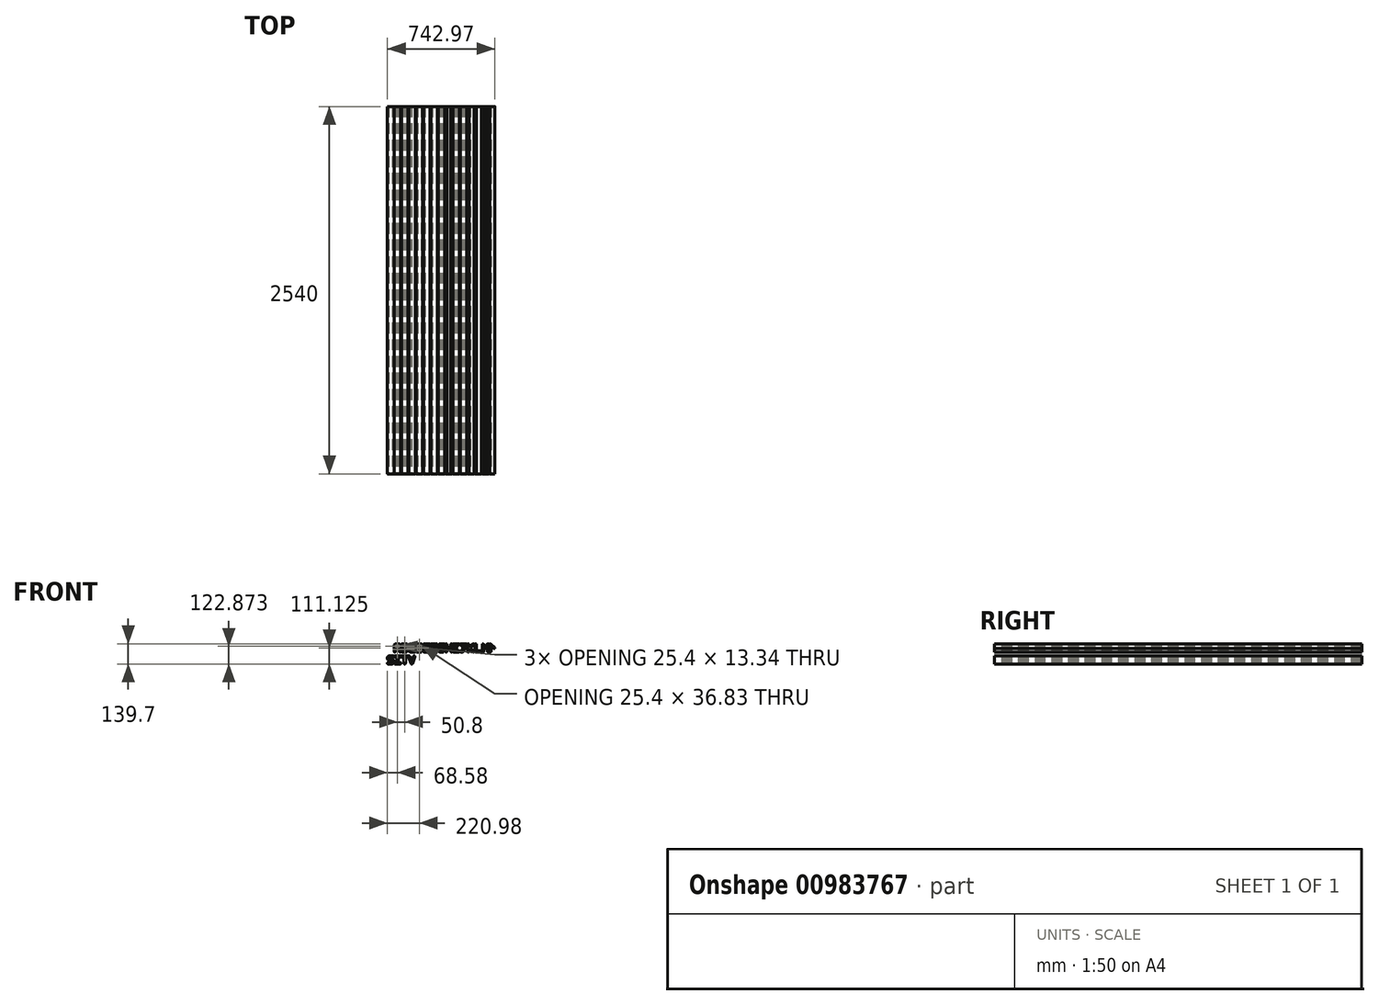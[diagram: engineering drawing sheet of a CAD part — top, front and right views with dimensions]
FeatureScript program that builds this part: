
annotation { "Feature Type Name" : "Feature", "Feature Type Description" : "" }
export const myFeature = defineFeature(function(context is Context, id is Id, definition is map)
    precondition{}
    {
        {
            var Q0;
            Q0=qCreatedBy(makeId("Front.planeOp"),FACE);
            var sketch = newSketch(context, id + "F0", { "sketchPlane" : qUnion([Q0])});
            skLineSegment(sketch, "E0", {"start": v(-40.64, 0) * mm, "end": v(-15.24, 0) * mm});
            skLineSegment(sketch, "E1", {"start": v(0, 0) * mm, "end": v(-15.24, 0) * mm, "construction": true});
            skLineSegment(sketch, "E2", {"start": v(-40.64, 0) * mm, "end": v(-45.72, 0) * mm, "construction": true});
            skLineSegment(sketch, "E3", {"start": v(99.06, -25.4) * mm, "end": v(99.06, -82.55) * mm, "construction": true});
            skLineSegment(sketch, "E4", {"start": v(99.06, -82.55) * mm, "end": v(144.78, -82.55) * mm, "construction": true});
            skPoint(sketch, "E5", {"position": v(121.92, -82.55) * mm});
            skLineSegment(sketch, "E6", {"start": v(99.06, -25.4) * mm, "end": v(144.78, -25.4) * mm, "construction": true});
            skLineSegment(sketch, "E7", {"start": v(144.78, -25.4) * mm, "end": v(144.78, -82.55) * mm, "construction": true});
            skLineSegment(sketch, "E8", {"start": v(99.39, -32.28) * mm, "end": v(117.17, -79.27) * mm});
            skLineSegment(sketch, "E9", {"start": v(117.17, -79.27) * mm, "end": v(126.67, -75.67) * mm, "construction": true});
            skLineSegment(sketch, "E10", {"start": v(126.67, -75.67) * mm, "end": v(108.9, -28.68) * mm});
            skLineSegment(sketch, "E11", {"start": v(108.9, -28.68) * mm, "end": v(99.39, -32.28) * mm, "construction": true});
            skPoint(sketch, "E12", {"position": v(104.14, -30.48) * mm});
            skPoint(sketch, "E13", {"position": v(121.92, -77.47) * mm});
            skArc(sketch, "E14", {"start": v(108.9, -28.68) * mm, "mid": v(102.34, -25.73) * mm, "end": v(99.39, -32.28) * mm});
            skArc(sketch, "E15", {"start": v(117.17, -79.27) * mm, "mid": v(123.72, -82.22) * mm, "end": v(126.67, -75.67) * mm});
            skLineSegment(sketch, "E16", {"start": v(121.92, -77.47) * mm, "end": v(121.92, -82.55) * mm, "construction": true});
            skArc(sketch, "E17", {"start": v(144.45, -32.28) * mm, "mid": v(141.5, -25.73) * mm, "end": v(134.95, -28.68) * mm});
            skLineSegment(sketch, "E18", {"start": v(134.95, -28.68) * mm, "end": v(144.45, -32.28) * mm});
            skLineSegment(sketch, "E19", {"start": v(144.45, -32.28) * mm, "end": v(126.67, -79.27) * mm});
            skLineSegment(sketch, "E20", {"start": v(134.95, -28.68) * mm, "end": v(121.92, -63.12) * mm});
            skLineSegment(sketch, "E21", {"start": v(121.92, -77.47) * mm, "end": v(126.67, -79.27) * mm, "construction": true});
            skLineSegment(sketch, "E22", {"start": v(-40.64, -82.55) * mm, "end": v(-15.24, -82.55) * mm});
            skLineSegment(sketch, "E23", {"start": v(-40.64, -72.4) * mm, "end": v(-15.24, -72.4) * mm});
            skLineSegment(sketch, "E24", {"start": v(-40.64, -72.4) * mm, "end": v(-40.64, -82.55) * mm, "construction": true});
            skArc(sketch, "E25", {"start": v(-40.64, -72.4) * mm, "mid": v(-45.72, -77.47) * mm, "end": v(-40.64, -82.55) * mm});
            skLineSegment(sketch, "E26", {"start": v(0, -82.55) * mm, "end": v(-15.24, -82.55) * mm, "construction": true});
            skLineSegment(sketch, "E27", {"start": v(0, -67.31) * mm, "end": v(0, -64.14) * mm});
            skLineSegment(sketch, "E28", {"start": v(-10.16, -67.31) * mm, "end": v(-10.16, -64.14) * mm});
            skArc(sketch, "E29", {"start": v(0, -64.14) * mm, "mid": v(-4.46, -53.36) * mm, "end": v(-15.24, -48.9) * mm});
            skLineSegment(sketch, "E30", {"start": v(0, -64.14) * mm, "end": v(-15.24, -64.14) * mm, "construction": true});
            skLineSegment(sketch, "E31", {"start": v(-15.24, -64.14) * mm, "end": v(-15.24, -48.9) * mm, "construction": true});
            skArc(sketch, "E32", {"start": v(-10.16, -64.14) * mm, "mid": v(-11.65, -60.54) * mm, "end": v(-15.24, -59.06) * mm});
            skLineSegment(sketch, "E33", {"start": v(-15.24, -48.9) * mm, "end": v(-30.48, -48.9) * mm});
            skLineSegment(sketch, "E34", {"start": v(-15.24, -59.06) * mm, "end": v(-30.48, -59.06) * mm});
            skLineSegment(sketch, "E35", {"start": v(-30.48, -59.06) * mm, "end": v(-30.48, -43.82) * mm, "construction": true});
            skLineSegment(sketch, "E36", {"start": v(-30.48, -43.82) * mm, "end": v(-45.72, -43.82) * mm, "construction": true});
            skLineSegment(sketch, "E37", {"start": v(-15.24, -82.55) * mm, "end": v(-15.24, -67.31) * mm, "construction": true});
            skLineSegment(sketch, "E38", {"start": v(0, -67.31) * mm, "end": v(-15.24, -67.31) * mm, "construction": true});
            skLineSegment(sketch, "E39", {"start": v(0, -67.31) * mm, "end": v(0, -82.55) * mm, "construction": true});
            skArc(sketch, "E40", {"start": v(-15.24, -82.55) * mm, "mid": v(-4.46, -78.09) * mm, "end": v(0, -67.31) * mm});
            skArc(sketch, "E41", {"start": v(-15.24, -72.4) * mm, "mid": v(-11.65, -70.9) * mm, "end": v(-10.16, -67.31) * mm});
            skArc(sketch, "E42", {"start": v(-45.72, -43.82) * mm, "mid": v(-41.26, -54.6) * mm, "end": v(-30.48, -59.06) * mm});
            skArc(sketch, "E43", {"start": v(-35.56, -43.82) * mm, "mid": v(-34.07, -47.4) * mm, "end": v(-30.48, -48.9) * mm});
            skLineSegment(sketch, "E44", {"start": v(-40.64, -82.55) * mm, "end": v(-45.72, -82.55) * mm, "construction": true});
            skLineSegment(sketch, "E45", {"start": v(-45.72, -43.82) * mm, "end": v(-45.72, -40.64) * mm});
            skLineSegment(sketch, "E46", {"start": v(-35.56, -43.82) * mm, "end": v(-35.56, -40.64) * mm});
            skLineSegment(sketch, "E47", {"start": v(-45.72, -40.64) * mm, "end": v(-30.48, -40.64) * mm, "construction": true});
            skLineSegment(sketch, "E48", {"start": v(-30.48, -40.64) * mm, "end": v(-30.48, -25.4) * mm, "construction": true});
            skArc(sketch, "E49", {"start": v(-30.48, -25.4) * mm, "mid": v(-41.26, -29.86) * mm, "end": v(-45.72, -40.64) * mm});
            skArc(sketch, "E50", {"start": v(-30.48, -35.56) * mm, "mid": v(-34.07, -37.05) * mm, "end": v(-35.56, -40.64) * mm});
            skLineSegment(sketch, "E51", {"start": v(-30.48, -35.56) * mm, "end": v(-5.08, -35.56) * mm});
            skLineSegment(sketch, "E52", {"start": v(-30.48, -25.4) * mm, "end": v(-5.08, -25.4) * mm});
            skLineSegment(sketch, "E53", {"start": v(-5.08, -25.4) * mm, "end": v(-5.08, -35.56) * mm, "construction": true});
            skArc(sketch, "E54", {"start": v(-5.08, -35.56) * mm, "mid": v(0, -30.48) * mm, "end": v(-5.08, -25.4) * mm});
            skLineSegment(sketch, "E55", {"start": v(7.62, -82.55) * mm, "end": v(43.18, -82.55) * mm});
            skLineSegment(sketch, "E56", {"start": v(43.18, -82.55) * mm, "end": v(43.18, -72.4) * mm, "construction": true});
            skLineSegment(sketch, "E57", {"start": v(7.62, -82.55) * mm, "end": v(7.62, -72.4) * mm, "construction": true});
            skLineSegment(sketch, "E58", {"start": v(7.62, -72.4) * mm, "end": v(20.32, -72.4) * mm});
            skLineSegment(sketch, "E59", {"start": v(43.18, -72.4) * mm, "end": v(30.48, -72.4) * mm});
            skArc(sketch, "E60", {"start": v(7.62, -72.4) * mm, "mid": v(2.54, -77.47) * mm, "end": v(7.62, -82.55) * mm});
            skArc(sketch, "E61", {"start": v(43.18, -82.55) * mm, "mid": v(48.26, -77.47) * mm, "end": v(43.18, -72.4) * mm});
            skLineSegment(sketch, "E62", {"start": v(20.32, -72.4) * mm, "end": v(30.48, -72.4) * mm, "construction": true});
            skLineSegment(sketch, "E63", {"start": v(20.32, -72.39) * mm, "end": v(20.32, -35.56) * mm});
            skLineSegment(sketch, "E64", {"start": v(20.32, -35.56) * mm, "end": v(7.62, -35.56) * mm});
            skLineSegment(sketch, "E65", {"start": v(7.62, -35.56) * mm, "end": v(7.62, -25.4) * mm, "construction": true});
            skLineSegment(sketch, "E66", {"start": v(7.62, -25.4) * mm, "end": v(43.18, -25.4) * mm});
            skLineSegment(sketch, "E67", {"start": v(43.18, -25.4) * mm, "end": v(43.18, -35.56) * mm, "construction": true});
            skLineSegment(sketch, "E68", {"start": v(43.18, -35.56) * mm, "end": v(30.48, -35.56) * mm});
            skLineSegment(sketch, "E69", {"start": v(30.48, -35.56) * mm, "end": v(30.48, -72.39) * mm});
            skArc(sketch, "E70", {"start": v(7.62, -25.4) * mm, "mid": v(2.54, -30.48) * mm, "end": v(7.62, -35.56) * mm});
            skArc(sketch, "E71", {"start": v(43.18, -35.56) * mm, "mid": v(48.26, -30.48) * mm, "end": v(43.18, -25.4) * mm});
            skLineSegment(sketch, "E72", {"start": v(7.62, -35.56) * mm, "end": v(7.62, -72.4) * mm, "construction": true});
            skLineSegment(sketch, "E73", {"start": v(43.18, -35.56) * mm, "end": v(43.18, -72.4) * mm, "construction": true});
            skLineSegment(sketch, "E74", {"start": v(0, -82.55) * mm, "end": v(7.62, -82.55) * mm, "construction": true});
            skLineSegment(sketch, "E75", {"start": v(43.18, -25.4) * mm, "end": v(55.88, -25.4) * mm, "construction": true});
            skLineSegment(sketch, "E76", {"start": v(55.88, -25.4) * mm, "end": v(55.88, -35.56) * mm, "construction": true});
            skLineSegment(sketch, "E77", {"start": v(55.88, -35.56) * mm, "end": v(68.58, -35.56) * mm});
            skLineSegment(sketch, "E78", {"start": v(68.58, -35.56) * mm, "end": v(78.74, -35.56) * mm, "construction": true});
            skLineSegment(sketch, "E79", {"start": v(78.74, -35.56) * mm, "end": v(91.44, -35.56) * mm});
            skLineSegment(sketch, "E80", {"start": v(91.44, -35.56) * mm, "end": v(91.44, -25.4) * mm, "construction": true});
            skLineSegment(sketch, "E81", {"start": v(91.44, -25.4) * mm, "end": v(55.88, -25.4) * mm});
            skLineSegment(sketch, "E82", {"start": v(68.58, -35.56) * mm, "end": v(68.58, -77.47) * mm});
            skLineSegment(sketch, "E83", {"start": v(68.58, -77.47) * mm, "end": v(78.74, -77.47) * mm, "construction": true});
            skLineSegment(sketch, "E84", {"start": v(78.74, -77.47) * mm, "end": v(78.74, -35.56) * mm});
            skArc(sketch, "E85", {"start": v(55.88, -25.4) * mm, "mid": v(50.8, -30.48) * mm, "end": v(55.88, -35.56) * mm});
            skArc(sketch, "E86", {"start": v(91.44, -35.56) * mm, "mid": v(96.52, -30.48) * mm, "end": v(91.44, -25.4) * mm});
            skArc(sketch, "E87", {"start": v(68.58, -77.47) * mm, "mid": v(73.66, -82.55) * mm, "end": v(78.74, -77.47) * mm});
            skLineSegment(sketch, "E88", {"start": v(-45.72, 0) * mm, "end": v(-45.72, -25.4) * mm, "construction": true});
            skLineSegment(sketch, "E89", {"start": v(-30.48, -25.4) * mm, "end": v(-45.72, -25.4) * mm, "construction": true});
            skLineSegment(sketch, "E90", {"start": v(-45.72, -25.4) * mm, "end": v(-45.72, -40.64) * mm, "construction": true});
            skLineSegment(sketch, "E91", {"start": v(91.44, -25.4) * mm, "end": v(99.06, -25.4) * mm, "construction": true});
            skLineSegment(sketch, "E92", {"start": v(45.72, 0) * mm, "end": v(0, 0) * mm, "construction": true});
            skLineSegment(sketch, "E93", {"start": v(45.72, 0) * mm, "end": v(45.72, 5.08) * mm, "construction": true});
            skLineSegment(sketch, "E94", {"start": v(45.72, 5.08) * mm, "end": v(45.72, 41.91) * mm});
            skLineSegment(sketch, "E95", {"start": v(45.72, 5.08) * mm, "end": v(35.56, 5.08) * mm, "construction": true});
            skLineSegment(sketch, "E96", {"start": v(0, 5.08) * mm, "end": v(10.16, 5.08) * mm, "construction": true});
            skPoint(sketch, "E97", {"position": v(5.08, 5.08) * mm});
            skArc(sketch, "E98", {"start": v(0, 5.08) * mm, "mid": v(5.08, 0) * mm, "end": v(10.16, 5.08) * mm});
            skLineSegment(sketch, "E99", {"start": v(0, 5.08) * mm, "end": v(0, 41.91) * mm});
            skLineSegment(sketch, "E100", {"start": v(0, 41.91) * mm, "end": v(15.24, 41.91) * mm, "construction": true});
            skLineSegment(sketch, "E101", {"start": v(0, 0) * mm, "end": v(0, 5.08) * mm, "construction": true});
            skArc(sketch, "E102", {"start": v(15.24, 57.15) * mm, "mid": v(4.46, 52.69) * mm, "end": v(0, 41.91) * mm});
            skLineSegment(sketch, "E103", {"start": v(15.24, 41.91) * mm, "end": v(15.24, 57.15) * mm, "construction": true});
            skLineSegment(sketch, "E104", {"start": v(15.24, 57.15) * mm, "end": v(30.48, 57.15) * mm});
            skLineSegment(sketch, "E105", {"start": v(30.48, 57.15) * mm, "end": v(30.48, 41.91) * mm, "construction": true});
            skLineSegment(sketch, "E106", {"start": v(30.48, 41.91) * mm, "end": v(45.72, 41.91) * mm, "construction": true});
            skArc(sketch, "E107", {"start": v(45.72, 41.91) * mm, "mid": v(41.26, 52.69) * mm, "end": v(30.48, 57.15) * mm});
            skArc(sketch, "E108", {"start": v(15.24, 47) * mm, "mid": v(11.65, 45.5) * mm, "end": v(10.16, 41.91) * mm});
            skArc(sketch, "E109", {"start": v(35.56, 41.91) * mm, "mid": v(34.07, 45.5) * mm, "end": v(30.48, 46.99) * mm});
            skLineSegment(sketch, "E110", {"start": v(15.24, 47) * mm, "end": v(30.48, 46.99) * mm});
            skLineSegment(sketch, "E111", {"start": v(10.16, 5.08) * mm, "end": v(10.16, 23.5) * mm});
            skLineSegment(sketch, "E112", {"start": v(35.56, 5.08) * mm, "end": v(35.56, 23.5) * mm});
            skLineSegment(sketch, "E113", {"start": v(35.56, 23.5) * mm, "end": v(10.16, 23.5) * mm});
            skLineSegment(sketch, "E114", {"start": v(10.16, 41.91) * mm, "end": v(10.16, 33.66) * mm});
            skLineSegment(sketch, "E115", {"start": v(10.16, 33.66) * mm, "end": v(35.56, 33.66) * mm});
            skLineSegment(sketch, "E116", {"start": v(35.56, 33.66) * mm, "end": v(35.56, 41.91) * mm});
            skLineSegment(sketch, "E117", {"start": v(10.16, 33.66) * mm, "end": v(10.16, 23.5) * mm, "construction": true});
            skLineSegment(sketch, "E118", {"start": v(35.56, 23.5) * mm, "end": v(35.56, 33.66) * mm, "construction": true});
            skArc(sketch, "E119", {"start": v(35.56, 5.08) * mm, "mid": v(40.64, 0) * mm, "end": v(45.72, 5.08) * mm});
            skLineSegment(sketch, "E120", {"start": v(45.72, 0) * mm, "end": v(50.8, 0) * mm, "construction": true});
            skLineSegment(sketch, "E121", {"start": v(50.8, 0) * mm, "end": v(50.8, 5.08) * mm, "construction": true});
            skLineSegment(sketch, "E122", {"start": v(50.8, 0) * mm, "end": v(55.88, 0) * mm, "construction": true});
            skLineSegment(sketch, "E123", {"start": v(55.88, 0) * mm, "end": v(55.88, 5.08) * mm, "construction": true});
            skLineSegment(sketch, "E124", {"start": v(55.88, 5.08) * mm, "end": v(50.8, 5.08) * mm, "construction": true});
            skArc(sketch, "E125", {"start": v(50.8, 5.08) * mm, "mid": v(52.29, 1.49) * mm, "end": v(55.88, 0) * mm});
            skLineSegment(sketch, "E126", {"start": v(50.8, 5.08) * mm, "end": v(50.8, 52.07) * mm});
            skLineSegment(sketch, "E127", {"start": v(50.8, 52.07) * mm, "end": v(55.88, 52.07) * mm, "construction": true});
            skLineSegment(sketch, "E128", {"start": v(55.88, 52.07) * mm, "end": v(55.88, 57.15) * mm, "construction": true});
            skArc(sketch, "E129", {"start": v(55.88, 57.15) * mm, "mid": v(52.29, 55.66) * mm, "end": v(50.8, 52.07) * mm});
            skLineSegment(sketch, "E130", {"start": v(55.88, 57.15) * mm, "end": v(81.28, 57.15) * mm});
            skLineSegment(sketch, "E131", {"start": v(81.28, 57.15) * mm, "end": v(81.28, 41.91) * mm, "construction": true});
            skArc(sketch, "E132", {"start": v(96.52, 41.91) * mm, "mid": v(92.06, 52.69) * mm, "end": v(81.28, 57.15) * mm});
            skLineSegment(sketch, "E133", {"start": v(81.28, 41.91) * mm, "end": v(96.52, 41.91) * mm, "construction": true});
            skLineSegment(sketch, "E134", {"start": v(96.52, 41.91) * mm, "end": v(96.52, 38.74) * mm});
            skLineSegment(sketch, "E135", {"start": v(81.28, 41.91) * mm, "end": v(81.28, 0) * mm, "construction": true});
            skLineSegment(sketch, "E136", {"start": v(96.52, 38.74) * mm, "end": v(81.28, 38.74) * mm, "construction": true});
            skArc(sketch, "E137", {"start": v(81.28, 23.5) * mm, "mid": v(87.5, 24.82) * mm, "end": v(92.64, 28.58) * mm, "construction": true});
            skLineSegment(sketch, "E138", {"start": v(55.88, 0) * mm, "end": v(81.28, 0) * mm});
            skLineSegment(sketch, "E139", {"start": v(81.28, 15.24) * mm, "end": v(96.52, 15.24) * mm, "construction": true});
            skArc(sketch, "E140", {"start": v(81.28, 0) * mm, "mid": v(92.06, 4.46) * mm, "end": v(96.52, 15.24) * mm});
            skLineSegment(sketch, "E141", {"start": v(96.52, 15.24) * mm, "end": v(96.52, 18.42) * mm});
            skLineSegment(sketch, "E142", {"start": v(96.52, 18.42) * mm, "end": v(81.28, 18.42) * mm, "construction": true});
            skArc(sketch, "E143", {"start": v(96.52, 18.42) * mm, "mid": v(95.52, 23.85) * mm, "end": v(92.64, 28.58) * mm});
            skLineSegment(sketch, "E144", {"start": v(60.96, 46.99) * mm, "end": v(60.96, 33.66) * mm});
            skLineSegment(sketch, "E145", {"start": v(60.96, 47) * mm, "end": v(81.28, 47) * mm});
            skLineSegment(sketch, "E146", {"start": v(60.96, 10.16) * mm, "end": v(81.28, 10.16) * mm});
            skLineSegment(sketch, "E147", {"start": v(50.8, 10.16) * mm, "end": v(60.96, 10.16) * mm, "construction": true});
            skLineSegment(sketch, "E148", {"start": v(60.96, 10.16) * mm, "end": v(60.96, 0) * mm, "construction": true});
            skLineSegment(sketch, "E149", {"start": v(60.96, 46.99) * mm, "end": v(60.96, 57.15) * mm, "construction": true});
            skArc(sketch, "E150", {"start": v(81.28, 10.16) * mm, "mid": v(84.87, 11.65) * mm, "end": v(86.36, 15.24) * mm});
            skArc(sketch, "E151", {"start": v(86.36, 41.91) * mm, "mid": v(84.87, 45.5) * mm, "end": v(81.28, 47) * mm});
            skLineSegment(sketch, "E152", {"start": v(86.36, 15.24) * mm, "end": v(86.36, 18.42) * mm});
            skLineSegment(sketch, "E153", {"start": v(86.36, 41.91) * mm, "end": v(86.36, 38.74) * mm});
            skArc(sketch, "E154", {"start": v(81.28, 33.66) * mm, "mid": v(84.87, 35.14) * mm, "end": v(86.36, 38.74) * mm});
            skArc(sketch, "E155", {"start": v(86.36, 18.42) * mm, "mid": v(84.87, 22) * mm, "end": v(81.28, 23.5) * mm});
            skLineSegment(sketch, "E156", {"start": v(81.28, 33.66) * mm, "end": v(60.96, 33.66) * mm});
            skLineSegment(sketch, "E157", {"start": v(81.28, 23.5) * mm, "end": v(60.96, 23.5) * mm});
            skLineSegment(sketch, "E158.trimOffspring", {"start": v(60.96, 23.5) * mm, "end": v(60.96, 10.16) * mm});
            skLineSegment(sketch, "E159", {"start": v(60.96, 23.5) * mm, "end": v(60.96, 33.66) * mm, "construction": true});
            skArc(sketch, "E160", {"start": v(92.64, 28.58) * mm, "mid": v(87.5, 32.33) * mm, "end": v(81.28, 33.66) * mm, "construction": true});
            skArc(sketch, "E161", {"start": v(92.64, 28.58) * mm, "mid": v(95.52, 33.3) * mm, "end": v(96.52, 38.74) * mm});
            skLineSegment(sketch, "E162", {"start": v(81.28, 0) * mm, "end": v(101.6, 0) * mm, "construction": true});
            skLineSegment(sketch, "E163", {"start": v(101.6, 0) * mm, "end": v(116.84, 0) * mm, "construction": true});
            skLineSegment(sketch, "E164", {"start": v(116.84, 0) * mm, "end": v(116.84, 15.24) * mm, "construction": true});
            skLineSegment(sketch, "E165", {"start": v(116.84, 15.24) * mm, "end": v(101.6, 15.24) * mm, "construction": true});
            skLineSegment(sketch, "E166", {"start": v(101.6, 15.24) * mm, "end": v(101.6, 0) * mm, "construction": true});
            skArc(sketch, "E167", {"start": v(101.6, 15.24) * mm, "mid": v(106.06, 4.46) * mm, "end": v(116.84, 0) * mm});
            skLineSegment(sketch, "E168", {"start": v(101.6, 15.24) * mm, "end": v(101.6, 41.91) * mm});
            skLineSegment(sketch, "E169", {"start": v(101.6, 41.91) * mm, "end": v(116.84, 41.91) * mm, "construction": true});
            skLineSegment(sketch, "E170", {"start": v(116.84, 41.91) * mm, "end": v(116.84, 57.15) * mm, "construction": true});
            skArc(sketch, "E171", {"start": v(116.84, 57.15) * mm, "mid": v(106.06, 52.69) * mm, "end": v(101.6, 41.91) * mm});
            skLineSegment(sketch, "E172", {"start": v(116.84, 0) * mm, "end": v(142.24, 0) * mm});
            skLineSegment(sketch, "E173", {"start": v(116.84, 57.15) * mm, "end": v(142.24, 57.15) * mm});
            skLineSegment(sketch, "E174", {"start": v(142.24, 57.15) * mm, "end": v(142.24, 47) * mm, "construction": true});
            skArc(sketch, "E175", {"start": v(142.24, 47) * mm, "mid": v(147.32, 52.07) * mm, "end": v(142.24, 57.15) * mm});
            skLineSegment(sketch, "E176", {"start": v(142.24, 47) * mm, "end": v(116.84, 47) * mm});
            skArc(sketch, "E177", {"start": v(116.84, 47) * mm, "mid": v(113.25, 45.5) * mm, "end": v(111.76, 41.91) * mm});
            skLineSegment(sketch, "E178", {"start": v(111.76, 41.91) * mm, "end": v(111.76, 15.24) * mm});
            skArc(sketch, "E179", {"start": v(111.76, 15.24) * mm, "mid": v(113.25, 11.65) * mm, "end": v(116.84, 10.16) * mm});
            skLineSegment(sketch, "E180", {"start": v(116.84, 10.16) * mm, "end": v(142.24, 10.16) * mm});
            skLineSegment(sketch, "E181", {"start": v(142.24, 10.16) * mm, "end": v(142.24, 0) * mm, "construction": true});
            skArc(sketch, "E182", {"start": v(142.24, 0) * mm, "mid": v(147.32, 5.08) * mm, "end": v(142.24, 10.16) * mm});
            skLineSegment(sketch, "E183", {"start": v(142.24, 0) * mm, "end": v(157.48, 0) * mm, "construction": true});
            skLineSegment(sketch, "E184", {"start": v(157.48, 0) * mm, "end": v(157.48, 5.08) * mm, "construction": true});
            skLineSegment(sketch, "E185", {"start": v(157.48, 5.08) * mm, "end": v(152.4, 5.08) * mm, "construction": true});
            skArc(sketch, "E186", {"start": v(152.4, 5.08) * mm, "mid": v(153.89, 1.49) * mm, "end": v(157.48, 0) * mm});
            skLineSegment(sketch, "E187", {"start": v(152.4, 5.08) * mm, "end": v(152.4, 52.07) * mm});
            skLineSegment(sketch, "E188", {"start": v(152.4, 52.07) * mm, "end": v(157.48, 52.07) * mm, "construction": true});
            skLineSegment(sketch, "E189", {"start": v(157.48, 52.07) * mm, "end": v(157.48, 57.15) * mm, "construction": true});
            skArc(sketch, "E190", {"start": v(157.48, 57.15) * mm, "mid": v(153.89, 55.66) * mm, "end": v(152.4, 52.07) * mm});
            skLineSegment(sketch, "E191", {"start": v(157.48, 57.15) * mm, "end": v(182.88, 57.15) * mm});
            skLineSegment(sketch, "E192", {"start": v(182.88, 57.15) * mm, "end": v(182.88, 41.91) * mm, "construction": true});
            skLineSegment(sketch, "E193", {"start": v(182.88, 41.91) * mm, "end": v(198.12, 41.91) * mm, "construction": true});
            skArc(sketch, "E194", {"start": v(198.12, 41.91) * mm, "mid": v(193.66, 52.69) * mm, "end": v(182.88, 57.15) * mm});
            skLineSegment(sketch, "E195", {"start": v(198.12, 41.91) * mm, "end": v(198.12, 15.24) * mm});
            skLineSegment(sketch, "E196", {"start": v(198.12, 15.24) * mm, "end": v(182.88, 15.24) * mm, "construction": true});
            skLineSegment(sketch, "E197", {"start": v(182.88, 15.24) * mm, "end": v(182.88, 0) * mm, "construction": true});
            skArc(sketch, "E198", {"start": v(182.88, 0) * mm, "mid": v(193.66, 4.46) * mm, "end": v(198.12, 15.24) * mm});
            skLineSegment(sketch, "E199", {"start": v(182.88, 0) * mm, "end": v(157.48, 0) * mm});
            skLineSegment(sketch, "E200", {"start": v(162.56, 47) * mm, "end": v(162.56, 10.16) * mm});
            skLineSegment(sketch, "E201", {"start": v(162.56, 10.16) * mm, "end": v(182.88, 10.16) * mm});
            skLineSegment(sketch, "E202", {"start": v(162.56, 10.16) * mm, "end": v(162.56, 0) * mm, "construction": true});
            skLineSegment(sketch, "E203", {"start": v(162.56, 10.16) * mm, "end": v(152.4, 10.16) * mm, "construction": true});
            skArc(sketch, "E204", {"start": v(182.88, 10.16) * mm, "mid": v(186.47, 11.65) * mm, "end": v(187.96, 15.24) * mm});
            skLineSegment(sketch, "E205", {"start": v(187.96, 15.24) * mm, "end": v(187.96, 41.91) * mm});
            skArc(sketch, "E206", {"start": v(187.96, 41.91) * mm, "mid": v(186.47, 45.5) * mm, "end": v(182.88, 47) * mm});
            skLineSegment(sketch, "E207", {"start": v(182.88, 47) * mm, "end": v(162.56, 47) * mm});
            skLineSegment(sketch, "E208", {"start": v(182.88, 0) * mm, "end": v(208.28, 0) * mm, "construction": true});
            skLineSegment(sketch, "E209", {"start": v(208.28, 0) * mm, "end": v(208.28, 5.08) * mm, "construction": true});
            skLineSegment(sketch, "E210", {"start": v(208.28, 5.08) * mm, "end": v(203.2, 5.08) * mm, "construction": true});
            skArc(sketch, "E211", {"start": v(203.2, 5.08) * mm, "mid": v(204.69, 1.49) * mm, "end": v(208.28, 0) * mm});
            skLineSegment(sketch, "E212", {"start": v(203.2, 5.08) * mm, "end": v(203.2, 52.07) * mm});
            skLineSegment(sketch, "E213", {"start": v(203.2, 52.07) * mm, "end": v(208.28, 52.07) * mm, "construction": true});
            skLineSegment(sketch, "E214", {"start": v(208.28, 52.07) * mm, "end": v(208.28, 57.15) * mm, "construction": true});
            skArc(sketch, "E215", {"start": v(208.28, 57.15) * mm, "mid": v(204.69, 55.66) * mm, "end": v(203.2, 52.07) * mm});
            skLineSegment(sketch, "E216", {"start": v(208.28, 57.15) * mm, "end": v(243.84, 57.15) * mm});
            skLineSegment(sketch, "E217", {"start": v(243.84, 57.15) * mm, "end": v(243.84, 47) * mm, "construction": true});
            skArc(sketch, "E218", {"start": v(243.84, 47) * mm, "mid": v(248.92, 52.07) * mm, "end": v(243.84, 57.15) * mm});
            skLineSegment(sketch, "E219", {"start": v(243.84, 47) * mm, "end": v(213.36, 47) * mm});
            skLineSegment(sketch, "E220", {"start": v(213.36, 47) * mm, "end": v(213.36, 33.66) * mm});
            skLineSegment(sketch, "E221", {"start": v(240.66, 23.5) * mm, "end": v(213.36, 23.5) * mm});
            skLineSegment(sketch, "E222", {"start": v(208.28, 0) * mm, "end": v(243.84, 0) * mm});
            skLineSegment(sketch, "E223", {"start": v(243.84, 0) * mm, "end": v(243.84, 10.16) * mm, "construction": true});
            skLineSegment(sketch, "E224", {"start": v(243.84, 10.16) * mm, "end": v(213.36, 10.16) * mm});
            skLineSegment(sketch, "E225", {"start": v(96.52, 38.74) * mm, "end": v(96.52, 28.58) * mm, "construction": true});
            skLineSegment(sketch, "E226", {"start": v(96.52, 28.58) * mm, "end": v(92.64, 28.58) * mm, "construction": true});
            skLineSegment(sketch, "E227", {"start": v(213.36, 10.16) * mm, "end": v(213.36, 23.5) * mm});
            skLineSegment(sketch, "E228", {"start": v(213.36, 33.65) * mm, "end": v(240.66, 33.65) * mm});
            skLineSegment(sketch, "E229", {"start": v(240.66, 33.66) * mm, "end": v(240.66, 23.5) * mm, "construction": true});
            skArc(sketch, "E230", {"start": v(240.66, 23.5) * mm, "mid": v(245.74, 28.58) * mm, "end": v(240.66, 33.66) * mm});
            skArc(sketch, "E231", {"start": v(243.84, 0) * mm, "mid": v(248.92, 5.08) * mm, "end": v(243.84, 10.16) * mm});
            skLineSegment(sketch, "E232", {"start": v(254, 5.08) * mm, "end": v(254, 52.07) * mm});
            skLineSegment(sketch, "E233", {"start": v(254, 52.07) * mm, "end": v(259.08, 52.07) * mm, "construction": true});
            skLineSegment(sketch, "E234", {"start": v(259.08, 52.07) * mm, "end": v(259.08, 57.15) * mm, "construction": true});
            skArc(sketch, "E235", {"start": v(259.08, 57.15) * mm, "mid": v(255.49, 55.66) * mm, "end": v(254, 52.07) * mm});
            skLineSegment(sketch, "E236", {"start": v(259.08, 57.15) * mm, "end": v(294.64, 57.15) * mm});
            skLineSegment(sketch, "E237", {"start": v(294.64, 57.15) * mm, "end": v(294.64, 46.99) * mm, "construction": true});
            skArc(sketch, "E238", {"start": v(294.64, 46.99) * mm, "mid": v(299.72, 52.07) * mm, "end": v(294.64, 57.15) * mm});
            skLineSegment(sketch, "E239", {"start": v(294.64, 46.99) * mm, "end": v(264.16, 46.99) * mm});
            skLineSegment(sketch, "E240", {"start": v(264.16, 46.99) * mm, "end": v(264.16, 33.65) * mm});
            skLineSegment(sketch, "E241", {"start": v(291.46, 23.5) * mm, "end": v(264.16, 23.5) * mm});
            skLineSegment(sketch, "E242", {"start": v(264.16, 5.08) * mm, "end": v(264.16, 23.5) * mm});
            skLineSegment(sketch, "E243", {"start": v(264.16, 33.65) * mm, "end": v(291.46, 33.65) * mm});
            skLineSegment(sketch, "E244", {"start": v(291.46, 33.65) * mm, "end": v(291.46, 23.5) * mm, "construction": true});
            skArc(sketch, "E245", {"start": v(291.46, 23.5) * mm, "mid": v(296.55, 28.57) * mm, "end": v(291.46, 33.65) * mm});
            skLineSegment(sketch, "E246", {"start": v(243.84, 0) * mm, "end": v(259.08, 0) * mm, "construction": true});
            skArc(sketch, "E247", {"start": v(254, 5.08) * mm, "mid": v(259.08, 0) * mm, "end": v(264.16, 5.08) * mm});
            skLineSegment(sketch, "E248", {"start": v(264.16, 33.65) * mm, "end": v(264.16, 23.5) * mm, "construction": true});
            skLineSegment(sketch, "E249", {"start": v(264.16, 5.08) * mm, "end": v(254, 5.08) * mm, "construction": true});
            skLineSegment(sketch, "E250", {"start": v(259.08, 0) * mm, "end": v(259.08, 5.08) * mm, "construction": true});
            skLineSegment(sketch, "E251", {"start": v(294.64, 57.15) * mm, "end": v(320.04, 57.15) * mm, "construction": true});
            skLineSegment(sketch, "E252", {"start": v(320.04, 57.15) * mm, "end": v(320.04, 41.9) * mm, "construction": true});
            skLineSegment(sketch, "E253", {"start": v(320.04, 41.9) * mm, "end": v(304.8, 41.9) * mm, "construction": true});
            skArc(sketch, "E254", {"start": v(320.04, 57.15) * mm, "mid": v(309.26, 52.69) * mm, "end": v(304.8, 41.9) * mm});
            skLineSegment(sketch, "E255", {"start": v(304.8, 41.9) * mm, "end": v(304.8, 15.24) * mm});
            skLineSegment(sketch, "E256", {"start": v(304.8, 15.24) * mm, "end": v(320.04, 15.24) * mm, "construction": true});
            skLineSegment(sketch, "E257", {"start": v(320.04, 15.24) * mm, "end": v(320.04, 0) * mm, "construction": true});
            skArc(sketch, "E258", {"start": v(304.8, 15.24) * mm, "mid": v(309.26, 4.46) * mm, "end": v(320.04, 0) * mm});
            skLineSegment(sketch, "E259", {"start": v(320.04, 57.15) * mm, "end": v(345.44, 57.15) * mm});
            skLineSegment(sketch, "E260", {"start": v(345.44, 57.15) * mm, "end": v(345.44, 46.99) * mm, "construction": true});
            skLineSegment(sketch, "E261", {"start": v(345.44, 46.99) * mm, "end": v(320.04, 46.99) * mm});
            skArc(sketch, "E262", {"start": v(345.44, 46.99) * mm, "mid": v(350.52, 52.07) * mm, "end": v(345.44, 57.15) * mm});
            skArc(sketch, "E263", {"start": v(320.04, 46.99) * mm, "mid": v(316.45, 45.5) * mm, "end": v(314.96, 41.9) * mm});
            skLineSegment(sketch, "E264", {"start": v(314.96, 41.9) * mm, "end": v(314.96, 15.24) * mm});
            skArc(sketch, "E265", {"start": v(314.96, 15.24) * mm, "mid": v(316.45, 11.65) * mm, "end": v(320.04, 10.16) * mm});
            skLineSegment(sketch, "E266", {"start": v(320.04, 0) * mm, "end": v(335.28, 0) * mm});
            skLineSegment(sketch, "E267", {"start": v(335.28, 0) * mm, "end": v(335.28, 15.24) * mm, "construction": true});
            skLineSegment(sketch, "E268", {"start": v(335.28, 15.24) * mm, "end": v(350.52, 15.24) * mm, "construction": true});
            skArc(sketch, "E269", {"start": v(335.28, 0) * mm, "mid": v(346.06, 4.46) * mm, "end": v(350.52, 15.24) * mm});
            skLineSegment(sketch, "E270", {"start": v(320.04, 10.16) * mm, "end": v(335.28, 10.16) * mm});
            skArc(sketch, "E271", {"start": v(335.28, 10.16) * mm, "mid": v(338.87, 11.65) * mm, "end": v(340.36, 15.24) * mm});
            skLineSegment(sketch, "E272", {"start": v(350.52, 15.24) * mm, "end": v(350.52, 23.5) * mm});
            skLineSegment(sketch, "E273", {"start": v(350.52, 23.5) * mm, "end": v(340.36, 23.5) * mm, "construction": true});
            skLineSegment(sketch, "E274", {"start": v(340.36, 15.24) * mm, "end": v(340.36, 23.5) * mm});
            skLineSegment(sketch, "E275", {"start": v(340.36, 33.65) * mm, "end": v(332.1, 33.65) * mm});
            skLineSegment(sketch, "E276", {"start": v(332.1, 33.65) * mm, "end": v(332.1, 23.5) * mm, "construction": true});
            skLineSegment(sketch, "E277", {"start": v(332.1, 23.5) * mm, "end": v(340.36, 23.5) * mm});
            skArc(sketch, "E278", {"start": v(332.1, 33.65) * mm, "mid": v(327.02, 28.57) * mm, "end": v(332.1, 23.5) * mm});
            skArc(sketch, "E279", {"start": v(350.52, 23.5) * mm, "mid": v(347.54, 30.68) * mm, "end": v(340.36, 33.65) * mm});
            skLineSegment(sketch, "E280", {"start": v(340.36, 23.5) * mm, "end": v(340.36, 33.65) * mm, "construction": true});
            skLineSegment(sketch, "E281", {"start": v(345.44, 57.15) * mm, "end": v(360.68, 57.15) * mm, "construction": true});
            skLineSegment(sketch, "E282", {"start": v(360.68, 57.15) * mm, "end": v(360.68, 52.07) * mm, "construction": true});
            skLineSegment(sketch, "E283", {"start": v(355.6, 52.07) * mm, "end": v(365.76, 52.07) * mm, "construction": true});
            skPoint(sketch, "E284", {"position": v(360.68, 52.07) * mm});
            skArc(sketch, "E285", {"start": v(365.76, 52.07) * mm, "mid": v(360.68, 57.15) * mm, "end": v(355.6, 52.07) * mm});
            skLineSegment(sketch, "E286", {"start": v(355.6, 52.07) * mm, "end": v(355.6, 5.08) * mm});
            skLineSegment(sketch, "E287", {"start": v(355.6, 5.08) * mm, "end": v(365.76, 5.08) * mm, "construction": true});
            skLineSegment(sketch, "E288", {"start": v(365.76, 5.08) * mm, "end": v(365.76, 23.5) * mm});
            skLineSegment(sketch, "E289", {"start": v(365.76, 23.5) * mm, "end": v(391.16, 23.5) * mm});
            skLineSegment(sketch, "E290", {"start": v(391.16, 23.5) * mm, "end": v(391.16, 5.08) * mm});
            skLineSegment(sketch, "E291", {"start": v(391.16, 5.08) * mm, "end": v(401.32, 5.08) * mm, "construction": true});
            skLineSegment(sketch, "E292", {"start": v(401.32, 5.08) * mm, "end": v(401.32, 52.07) * mm});
            skLineSegment(sketch, "E293", {"start": v(401.32, 52.07) * mm, "end": v(391.16, 52.07) * mm, "construction": true});
            skLineSegment(sketch, "E294", {"start": v(391.16, 52.07) * mm, "end": v(391.16, 33.65) * mm});
            skLineSegment(sketch, "E295", {"start": v(391.16, 33.65) * mm, "end": v(365.76, 33.65) * mm});
            skLineSegment(sketch, "E296", {"start": v(365.76, 33.65) * mm, "end": v(365.76, 52.07) * mm});
            skArc(sketch, "E297", {"start": v(355.6, 5.08) * mm, "mid": v(360.68, 0) * mm, "end": v(365.76, 5.08) * mm});
            skArc(sketch, "E298", {"start": v(391.16, 5.08) * mm, "mid": v(396.24, 0) * mm, "end": v(401.32, 5.08) * mm});
            skArc(sketch, "E299", {"start": v(401.32, 52.07) * mm, "mid": v(396.24, 57.15) * mm, "end": v(391.16, 52.07) * mm});
            skLineSegment(sketch, "E300", {"start": v(396.24, 52.07) * mm, "end": v(396.24, 57.15) * mm, "construction": true});
            skLineSegment(sketch, "E301", {"start": v(396.24, 57.15) * mm, "end": v(411.48, 57.15) * mm, "construction": true});
            skLineSegment(sketch, "E302", {"start": v(411.48, 57.15) * mm, "end": v(411.48, 46.99) * mm, "construction": true});
            skLineSegment(sketch, "E303", {"start": v(411.48, 46.99) * mm, "end": v(424.18, 46.99) * mm});
            skLineSegment(sketch, "E304", {"start": v(424.18, 46.99) * mm, "end": v(424.18, 10.16) * mm});
            skLineSegment(sketch, "E305", {"start": v(424.18, 10.16) * mm, "end": v(411.48, 10.16) * mm});
            skLineSegment(sketch, "E306", {"start": v(411.48, 10.16) * mm, "end": v(411.48, 0) * mm, "construction": true});
            skLineSegment(sketch, "E307", {"start": v(411.48, 0) * mm, "end": v(447.04, 0) * mm});
            skLineSegment(sketch, "E308", {"start": v(447.04, 0) * mm, "end": v(447.04, 10.16) * mm, "construction": true});
            skLineSegment(sketch, "E309", {"start": v(447.04, 10.16) * mm, "end": v(434.34, 10.16) * mm});
            skLineSegment(sketch, "E310", {"start": v(434.34, 10.16) * mm, "end": v(434.34, 47) * mm});
            skLineSegment(sketch, "E311", {"start": v(434.34, 47) * mm, "end": v(447.04, 47) * mm});
            skLineSegment(sketch, "E312", {"start": v(447.04, 47) * mm, "end": v(447.04, 57.15) * mm, "construction": true});
            skLineSegment(sketch, "E313", {"start": v(447.04, 57.15) * mm, "end": v(411.48, 57.15) * mm});
            skArc(sketch, "E314", {"start": v(411.48, 10.16) * mm, "mid": v(406.4, 5.08) * mm, "end": v(411.48, 0) * mm});
            skArc(sketch, "E315", {"start": v(447.04, 0) * mm, "mid": v(452.12, 5.08) * mm, "end": v(447.04, 10.16) * mm});
            skArc(sketch, "E316", {"start": v(447.04, 47) * mm, "mid": v(452.12, 52.07) * mm, "end": v(447.04, 57.15) * mm});
            skArc(sketch, "E317", {"start": v(411.48, 57.15) * mm, "mid": v(406.4, 52.07) * mm, "end": v(411.48, 47) * mm});
            skLineSegment(sketch, "E318", {"start": v(447.04, 0) * mm, "end": v(462.28, 0) * mm, "construction": true});
            skLineSegment(sketch, "E319", {"start": v(462.28, 0) * mm, "end": v(462.28, 10.16) * mm, "construction": true});
            skArc(sketch, "E320", {"start": v(462.28, 10.16) * mm, "mid": v(457.2, 5.08) * mm, "end": v(462.28, 0) * mm});
            skLineSegment(sketch, "E321", {"start": v(462.28, 0) * mm, "end": v(469.9, 0) * mm});
            skLineSegment(sketch, "E322", {"start": v(469.9, 0) * mm, "end": v(469.9, 15.24) * mm, "construction": true});
            skLineSegment(sketch, "E323", {"start": v(469.9, 15.24) * mm, "end": v(485.14, 15.24) * mm, "construction": true});
            skArc(sketch, "E324", {"start": v(469.9, 0) * mm, "mid": v(480.68, 4.46) * mm, "end": v(485.14, 15.24) * mm});
            skLineSegment(sketch, "E325", {"start": v(462.28, 10.16) * mm, "end": v(469.9, 10.16) * mm});
            skArc(sketch, "E326", {"start": v(469.9, 10.16) * mm, "mid": v(473.5, 11.65) * mm, "end": v(474.98, 15.24) * mm});
            skLineSegment(sketch, "E327", {"start": v(485.14, 15.24) * mm, "end": v(485.14, 47) * mm});
            skLineSegment(sketch, "E328", {"start": v(474.98, 46.99) * mm, "end": v(474.98, 15.24) * mm});
            skLineSegment(sketch, "E329", {"start": v(485.14, 47) * mm, "end": v(497.84, 47) * mm});
            skLineSegment(sketch, "E330", {"start": v(497.84, 47) * mm, "end": v(497.84, 57.15) * mm, "construction": true});
            skLineSegment(sketch, "E331", {"start": v(497.84, 57.15) * mm, "end": v(462.28, 57.15) * mm});
            skLineSegment(sketch, "E332", {"start": v(462.28, 57.15) * mm, "end": v(462.28, 47) * mm, "construction": true});
            skLineSegment(sketch, "E333", {"start": v(462.28, 46.99) * mm, "end": v(474.98, 46.99) * mm});
            skArc(sketch, "E334", {"start": v(462.28, 57.15) * mm, "mid": v(457.2, 52.07) * mm, "end": v(462.28, 47) * mm});
            skArc(sketch, "E335", {"start": v(497.84, 47) * mm, "mid": v(502.92, 52.07) * mm, "end": v(497.84, 57.15) * mm});
            skLineSegment(sketch, "E336", {"start": v(497.84, 57.15) * mm, "end": v(513.08, 57.15) * mm, "construction": true});
            skLineSegment(sketch, "E337", {"start": v(513.08, 57.15) * mm, "end": v(513.08, 52.07) * mm, "construction": true});
            skLineSegment(sketch, "E338", {"start": v(508, 52.07) * mm, "end": v(518.16, 52.07) * mm, "construction": true});
            skPoint(sketch, "E339", {"position": v(513.08, 52.07) * mm});
            skArc(sketch, "E340", {"start": v(518.16, 52.07) * mm, "mid": v(513.08, 57.15) * mm, "end": v(508, 52.07) * mm});
            skLineSegment(sketch, "E341", {"start": v(508, 52.07) * mm, "end": v(508, 5.08) * mm});
            skLineSegment(sketch, "E342", {"start": v(508, 5.08) * mm, "end": v(518.16, 5.08) * mm, "construction": true});
            skLineSegment(sketch, "E343", {"start": v(508, 28.57) * mm, "end": v(518.16, 28.57) * mm, "construction": true});
            skCircle(sketch, "E344", {"center": v(518.16, 28.57) * mm, "radius": 5.08 * mm, "construction": true});
            skLineSegment(sketch, "E345", {"start": v(515.06, 32.6) * mm, "end": v(521.26, 24.55) * mm, "construction": true});
            skLineSegment(sketch, "E346", {"start": v(515.06, 32.6) * mm, "end": v(545.54, 56.1) * mm});
            skLineSegment(sketch, "E347", {"start": v(545.54, 56.1) * mm, "end": v(551.74, 48.05) * mm, "construction": true});
            skLineSegment(sketch, "E348", {"start": v(551.74, 48.05) * mm, "end": v(521.26, 24.55) * mm});
            skPoint(sketch, "E349", {"position": v(548.64, 52.07) * mm});
            skArc(sketch, "E350", {"start": v(551.74, 48.05) * mm, "mid": v(552.66, 55.17) * mm, "end": v(545.54, 56.1) * mm});
            skLineSegment(sketch, "E351", {"start": v(548.64, 52.07) * mm, "end": v(548.64, 57.15) * mm, "construction": true});
            skLineSegment(sketch, "E352", {"start": v(548.64, 57.15) * mm, "end": v(513.08, 57.15) * mm, "construction": true});
            skArc(sketch, "E353", {"start": v(508, 5.08) * mm, "mid": v(513.08, 0) * mm, "end": v(518.16, 5.08) * mm});
            skLineSegment(sketch, "E354", {"start": v(521.26, 32.6) * mm, "end": v(515.06, 24.55) * mm, "construction": true});
            skLineSegment(sketch, "E355", {"start": v(515.06, 24.55) * mm, "end": v(545.54, 1.06) * mm});
            skLineSegment(sketch, "E356", {"start": v(545.54, 1.06) * mm, "end": v(551.74, 9.1) * mm, "construction": true});
            skLineSegment(sketch, "E357", {"start": v(551.74, 9.1) * mm, "end": v(521.26, 32.6) * mm});
            skArc(sketch, "E358", {"start": v(545.54, 1.06) * mm, "mid": v(552.66, 1.98) * mm, "end": v(551.74, 9.1) * mm});
            skLineSegment(sketch, "E359", {"start": v(548.64, 5.08) * mm, "end": v(548.64, 0) * mm, "construction": true});
            skLineSegment(sketch, "E360", {"start": v(548.64, 0) * mm, "end": v(513.08, 0) * mm, "construction": true});
            skPoint(sketch, "E360.endSnap0", {"position": v(513.08, 0) * mm});
            skLineSegment(sketch, "E361", {"start": v(518.16, 5.08) * mm, "end": v(518.16, 22.16) * mm});
            skLineSegment(sketch, "E362", {"start": v(518.16, 52.07) * mm, "end": v(518.16, 34.99) * mm});
            skLineSegment(sketch, "E363", {"start": v(548.64, 57.15) * mm, "end": v(563.88, 57.15) * mm, "construction": true});
            skArc(sketch, "E364", {"start": v(568.96, 52.07) * mm, "mid": v(563.88, 57.15) * mm, "end": v(558.8, 52.07) * mm});
            skLineSegment(sketch, "E365", {"start": v(563.88, 52.07) * mm, "end": v(563.88, 57.15) * mm, "construction": true});
            skLineSegment(sketch, "E366", {"start": v(558.8, 52.07) * mm, "end": v(568.96, 52.07) * mm, "construction": true});
            skLineSegment(sketch, "E367", {"start": v(558.8, 52.07) * mm, "end": v(558.8, 5.08) * mm});
            skLineSegment(sketch, "E368", {"start": v(568.96, 52.07) * mm, "end": v(568.96, 10.16) * mm});
            skArc(sketch, "E369", {"start": v(558.8, 5.08) * mm, "mid": v(560.29, 1.49) * mm, "end": v(563.88, 0) * mm});
            skLineSegment(sketch, "E370", {"start": v(558.8, 5.08) * mm, "end": v(563.88, 5.08) * mm, "construction": true});
            skLineSegment(sketch, "E371", {"start": v(563.88, 5.08) * mm, "end": v(563.88, 0) * mm, "construction": true});
            skLineSegment(sketch, "E372", {"start": v(563.88, 0) * mm, "end": v(599.44, 0) * mm});
            skLineSegment(sketch, "E373", {"start": v(599.44, 0) * mm, "end": v(599.44, 10.16) * mm, "construction": true});
            skLineSegment(sketch, "E374", {"start": v(599.44, 10.16) * mm, "end": v(568.96, 10.16) * mm});
            skArc(sketch, "E375", {"start": v(599.44, 0) * mm, "mid": v(604.52, 5.08) * mm, "end": v(599.44, 10.16) * mm});
            skLineSegment(sketch, "E376", {"start": v(599.44, 0) * mm, "end": v(614.68, 0) * mm, "construction": true});
            skLineSegment(sketch, "E377", {"start": v(614.68, 0) * mm, "end": v(614.68, 5.08) * mm, "construction": true});
            skLineSegment(sketch, "E378", {"start": v(614.68, 0) * mm, "end": v(650.24, 0) * mm, "construction": true});
            skLineSegment(sketch, "E379", {"start": v(650.24, 0) * mm, "end": v(650.24, 5.08) * mm, "construction": true});
            skArc(sketch, "E380", {"start": v(645.16, 5.08) * mm, "mid": v(650.24, 0) * mm, "end": v(655.32, 5.08) * mm});
            skLineSegment(sketch, "E381", {"start": v(655.32, 5.08) * mm, "end": v(645.16, 5.08) * mm, "construction": true});
            skLineSegment(sketch, "E382", {"start": v(655.32, 5.08) * mm, "end": v(655.32, 52.07) * mm});
            skCircle(sketch, "E383", {"center": v(650.24, 52.07) * mm, "radius": 5.08 * mm});
            skLineSegment(sketch, "E384", {"start": v(655.32, 52.07) * mm, "end": v(650.24, 52.07) * mm, "construction": true});
            skCircle(sketch, "E385", {"center": v(632.46, 27.94) * mm, "radius": 5.08 * mm});
            skLineSegment(sketch, "E386", {"start": v(610.67, 47.68) * mm, "end": v(628.45, 24.82) * mm});
            skLineSegment(sketch, "E387", {"start": v(628.45, 24.82) * mm, "end": v(636.47, 31.06) * mm, "construction": true});
            skLineSegment(sketch, "E388", {"start": v(636.47, 31.06) * mm, "end": v(618.69, 53.92) * mm});
            skLineSegment(sketch, "E389", {"start": v(646.15, 55.08) * mm, "end": v(628.37, 30.95) * mm});
            skLineSegment(sketch, "E390", {"start": v(628.37, 30.95) * mm, "end": v(636.55, 24.93) * mm, "construction": true});
            skLineSegment(sketch, "E391", {"start": v(636.55, 24.93) * mm, "end": v(654.33, 49.06) * mm});
            skLineSegment(sketch, "E392", {"start": v(609.6, 27.94) * mm, "end": v(632.46, 27.94) * mm, "construction": true});
            skLineSegment(sketch, "E393", {"start": v(645.16, 5.08) * mm, "end": v(645.16, 36.61) * mm});
            skLineSegment(sketch, "E394", {"start": v(655.32, 52.07) * mm, "end": v(660.4, 52.07) * mm, "construction": true});
            skArc(sketch, "E395", {"start": v(609.6, 5.08) * mm, "mid": v(614.68, 0) * mm, "end": v(619.76, 5.08) * mm});
            skLineSegment(sketch, "E396", {"start": v(609.6, 5.08) * mm, "end": v(619.76, 5.08) * mm, "construction": true});
            skLineSegment(sketch, "E397", {"start": v(609.6, 5.08) * mm, "end": v(609.6, 50.8) * mm});
            skLineSegment(sketch, "E398", {"start": v(609.6, 50.8) * mm, "end": v(614.68, 50.8) * mm, "construction": true});
            skCircle(sketch, "E399", {"center": v(614.68, 50.8) * mm, "radius": 5.08 * mm});
            skLineSegment(sketch, "E400", {"start": v(610.67, 47.68) * mm, "end": v(618.69, 53.92) * mm, "construction": true});
            skLineSegment(sketch, "E401", {"start": v(646.15, 55.08) * mm, "end": v(654.33, 49.06) * mm, "construction": true});
            skLineSegment(sketch, "E402", {"start": v(619.76, 5.08) * mm, "end": v(619.76, 36.25) * mm});
            skPoint(sketch, "E402.endSnap0", {"position": v(619.56, 36.25) * mm});
            skLineSegment(sketch, "E403", {"start": v(660.4, 52.07) * mm, "end": v(665.48, 52.07) * mm, "construction": true});
            skCircle(sketch, "E404", {"center": v(665.48, 52.07) * mm, "radius": 5.08 * mm});
            skLineSegment(sketch, "E405", {"start": v(660.4, 52.07) * mm, "end": v(660.4, 5.08) * mm});
            skLineSegment(sketch, "E406", {"start": v(660.4, 5.08) * mm, "end": v(670.56, 5.08) * mm, "construction": true});
            skLineSegment(sketch, "E407", {"start": v(670.56, 5.08) * mm, "end": v(670.56, 52.07) * mm});
            skArc(sketch, "E408", {"start": v(660.4, 5.08) * mm, "mid": v(665.48, 0) * mm, "end": v(670.56, 5.08) * mm});
            skLineSegment(sketch, "E409", {"start": v(662.12, 48.26) * mm, "end": v(688.82, 24.76) * mm});
            skLineSegment(sketch, "E410", {"start": v(662.12, 48.26) * mm, "end": v(668.84, 55.88) * mm, "construction": true});
            skLineSegment(sketch, "E411", {"start": v(668.84, 55.88) * mm, "end": v(695.53, 32.39) * mm});
            skCircle(sketch, "E412", {"center": v(692.17, 28.58) * mm, "radius": 5.08 * mm});
            skLineSegment(sketch, "E413", {"start": v(688.82, 24.76) * mm, "end": v(695.53, 32.39) * mm, "construction": true});
            skLineSegment(sketch, "E414", {"start": v(665.48, 5.08) * mm, "end": v(665.48, 0) * mm, "construction": true});
            skLineSegment(sketch, "E415", {"start": v(692.17, 28.58) * mm, "end": v(692.17, 23.5) * mm, "construction": true});
            skLineSegment(sketch, "E416", {"start": v(692.17, 23.5) * mm, "end": v(665.48, 0) * mm, "construction": true});
            skSolve(sketch);
        }
        {
            var Q0;
            Q0=qSketchRegion(id+"F0",true);
            extrude(context, id + "F1", {"entities" : qUnion([Q0]), "oppositeDirection" : true, "depth" : 2540 * mm, "offsetDistance" : 25.4 * mm});
        }
    });
